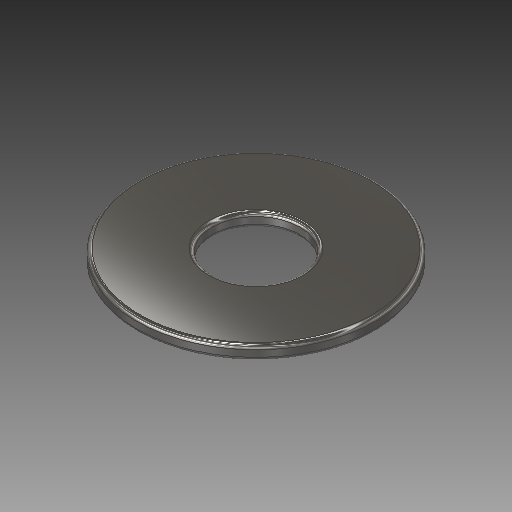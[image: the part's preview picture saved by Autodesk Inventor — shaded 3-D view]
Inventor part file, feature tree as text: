
AUTODESK INVENTOR PART (.ipt)
format: ipt  version: 2018 (Build 220112000, 112)  size: 142,848 bytes
history: native  units: mm
features: other x1, revolve x1, fillet x1, sketch x1
ambient origin geometry x8: Origin, YZ Plane, XZ Plane, XY Plane, X Axis, Y Axis, Z Axis, Center Point
bodies: Body1 (feature_tree)
feature tree (4):
  other  "Твердое тело1"
  revolve  "Вращение1"
  fillet  "Сопряжение3"  Radius=26.0mm
  sketch  "Эскиз1"
